# Revit family: Sechskantmutter VA
name_source: partatom
category: HLS-Bauteile
revit_build: Autodesk Revit 2017 (Build: 20190507_1515(x64)
units: mm (PartAtom-declared; Revit-internal decimal feet)

## family parameters
Arbeitsebenenbasiert = Ja
Beim Laden mit Abzugskörper schneiden = Nein
Bemaßung runder Anschluss = Durchmesser verwenden
Gemeinsam genutzt = Ja
Immer vertikal = Nein
Raumberechnungspunkt = Nein
Teiletyp = Normal

## types (10) — shared parameters
Fabrikat = MEFA
Firma = MEFA Befestigungs- und Montagesysteme GmbH
Material = Edelstahl
Mengeneinheit = St
Vorgabe-Ansicht = 1219 mm
vpe = 100 St

## per-type parameters (varying)
| type | Artikelnummer | D | EAN | F2 | Gewicht | Gewicht pro Bauteil | H | Kurztext1 | Kurztext2 |
| Sechskantmutter M16 V2A | 4128016 | 7 mm  [stored 0.0229659 ft] | 4250928438966 | 12 mm  [stored 0.0393701 ft] | 0.04 kg | 0.04 kg | 13 mm | Sechskantmutter V2A | M16 SW 24 |
| Sechskantmutter M10 V2A | 4128010 | 4 mm  [stored 0.0131234 ft] | 4250928438942 | 9 mm  [stored 0.0295276 ft] | 0.01 kg | 0.01 kg | 8 mm  [stored 0.0262467 ft] | Sechskantmutter V2A | M10 SW 17 |
| Sechskantmutter M12 V2A | 4128012 | 5 mm  [stored 0.0164042 ft] | 4250928438959 | 9 mm  [stored 0.0295276 ft] | 0.02 kg | 0.02 kg | 10 mm  [stored 0.0328084 ft] | Sechskantmutter V2A | M12 SW 19 |
| Sechskantmutter M 8 V4A | 4128108 | 3 mm  [stored 0.00984252 ft] | 4250928438980 | 7 mm  [stored 0.0229659 ft] | 0.01 kg | 0.01 kg | 7 mm  [stored 0.0229659 ft] | Sechskantmutter V4A | M8 SW 13 |
| Sechskantmutter M 6 V2A | 4128106 | 3 mm  [stored 0.00984252 ft] | 4250928438973 | 5 mm  [stored 0.0164042 ft] | 0.00 kg | 0.00 kg | 5 mm  [stored 0.0164042 ft] | Sechskantmutter V2A | M6 SW 10 |
| Sechskantmutter M 6 V4A | 4128006 | 3 mm  [stored 0.00984252 ft] | 4250928438928 | 5 mm  [stored 0.0164042 ft] | 0.00 kg | 0.00 kg | 5 mm  [stored 0.0164042 ft] | Sechskantmutter V4A | M6 SW 10 |
| Sechskantmutter M 8 V2A | 4128008 | 3 mm  [stored 0.00984252 ft] | 4250928438935 | 7 mm  [stored 0.0229659 ft] | 0.01 kg | 0.01 kg | 7 mm  [stored 0.0229659 ft] | Sechskantmutter V2A | M8 SW 13 |
| Sechskantmutter M10 V4A | 4128110 | 4 mm  [stored 0.0131234 ft] | 4250928438997 | 9 mm  [stored 0.0295276 ft] | 0.01 kg | 0.01 kg | 8 mm  [stored 0.0262467 ft] | Sechskantmutter V4A | M10 SW 17 |
| Sechskantmutter M12 V4A | 4128112 | 5 mm  [stored 0.0164042 ft] | 4250928439000 | 9 mm  [stored 0.0295276 ft] | 0.02 kg | 0.02 kg | 10 mm  [stored 0.0328084 ft] | Sechskantmutter V4A | M12 SW 19 |
| Sechskantmutter M16 V4A | 4128116 | 7 mm  [stored 0.0229659 ft] | 4250928439017 | 12 mm  [stored 0.0393701 ft] | 0.04 kg | 0.04 kg | 13 mm | Sechskantmutter V4A | M16 SW 24 |

note: [stored X ft] marks values corroborated as IEEE doubles in the binary element streams (Revit-internal decimal feet)

## geometry (parser evidence)
native form markers: Sweep x3
no freeform markers — native parametric forms only
